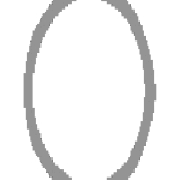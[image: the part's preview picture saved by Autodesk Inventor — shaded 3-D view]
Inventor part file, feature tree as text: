
AUTODESK INVENTOR PART (.ipt)
format: ipt  version: 2021 (Build 250183000, 183)  size: 112,128 bytes
history: native  units: in
note: dims shown in document units (in); Inventor stores cm internally (conversion verified against a paired STEP export)
features: other x4, sketch x3, plane x1
ambient origin geometry x8: Origin, YZ Plane, XZ Plane, XY Plane, X Axis, Y Axis, Z Axis, Center Point
bodies: Solid1 (feature_tree), Body (feature_tree)
feature tree (8):
  other  "Driven Length"
  other  "Frame Generator"
  other  "Start Plane"
  other  "End Plane"
  sketch  "Sketch"  dims[d2=5.831in d4=-0.0in d5=5.831in d6=0.12in d7=0.0in d8=90.0deg d9=5.831in]
  sketch  "Sketch2"  dims[d0=1.0in]
  plane  "Work Plane3"
  sketch  "Sketch3"  dims[d1=0.065in]
